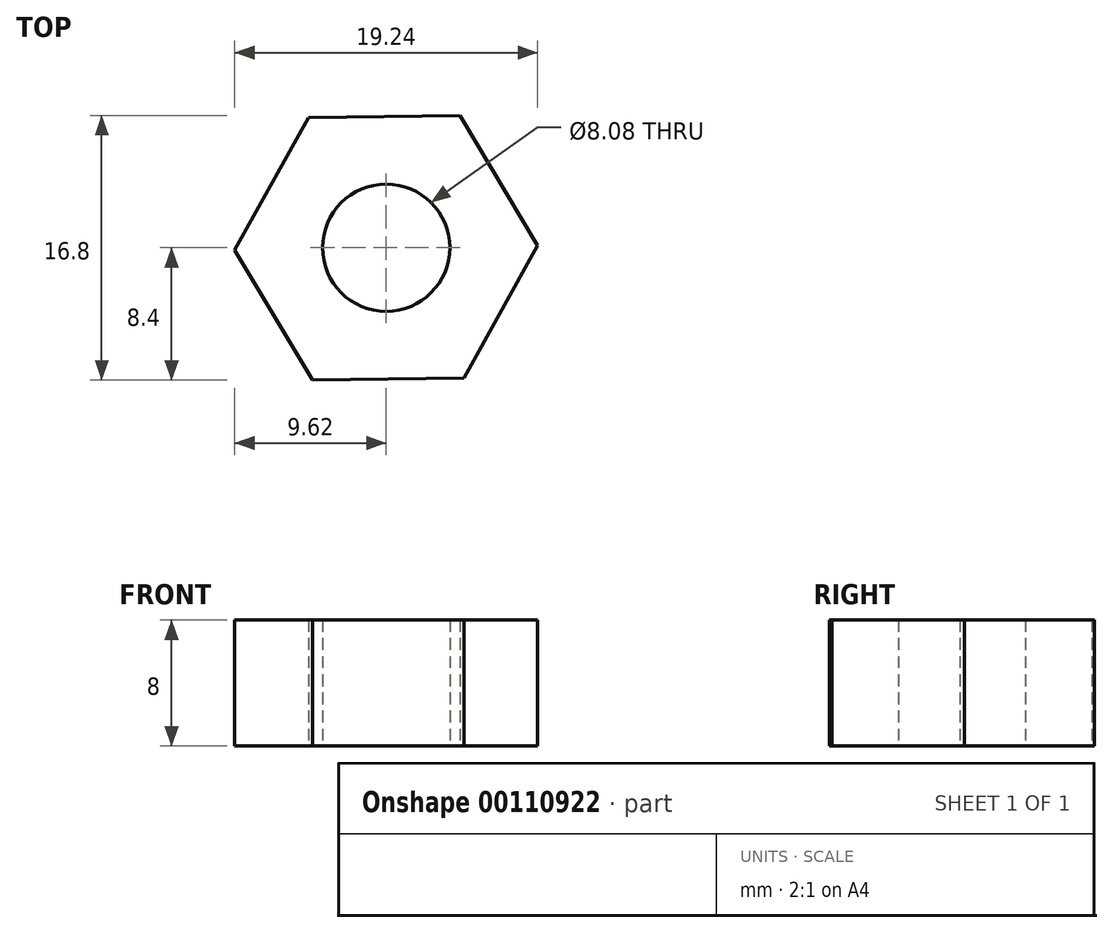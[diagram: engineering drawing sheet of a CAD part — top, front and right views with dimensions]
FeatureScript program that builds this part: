
annotation { "Feature Type Name" : "Feature", "Feature Type Description" : "" }
export const myFeature = defineFeature(function(context is Context, id is Id, definition is map)
    precondition{}
    {
        {
            var Q0;
            Q0=qCreatedBy(makeId("Top.planeOp"),FACE);
            var sketch = newSketch(context, id + "F0", { "sketchPlane" : qUnion([Q0])});
            skCircle(sketch, "E0.cCircle", {"center": v(0, 0) * mm, "radius": 8.33 * mm, "construction": true});
            skLineSegment(sketch, "E0.0", {"start": v(4.69, 8.4) * mm, "end": v(9.62, 0.14) * mm});
            skLineSegment(sketch, "E0.1", {"start": v(9.62, 0.14) * mm, "end": v(4.93, -8.26) * mm});
            skLineSegment(sketch, "E0.2", {"start": v(4.93, -8.26) * mm, "end": v(-4.69, -8.4) * mm});
            skLineSegment(sketch, "E0.3", {"start": v(-4.69, -8.4) * mm, "end": v(-9.62, -0.14) * mm});
            skLineSegment(sketch, "E0.4", {"start": v(-9.62, -0.14) * mm, "end": v(-4.93, 8.26) * mm});
            skLineSegment(sketch, "E0.5", {"start": v(-4.93, 8.26) * mm, "end": v(4.69, 8.4) * mm});
            skPoint(sketch, "E0.0.midPoint", {"position": v(7.15, 4.27) * mm});
            skCircle(sketch, "E1", {"center": v(0, 0) * mm, "radius": 4.04 * mm});
            skSolve(sketch);
        }
        {
            var Q0;
            Q0 = qSketchRegion(id + "F0", true);
            extrude(context, id + "F1", {"entities" : qUnion([Q0]), "depth" : 8 * mm});
        }
    });
